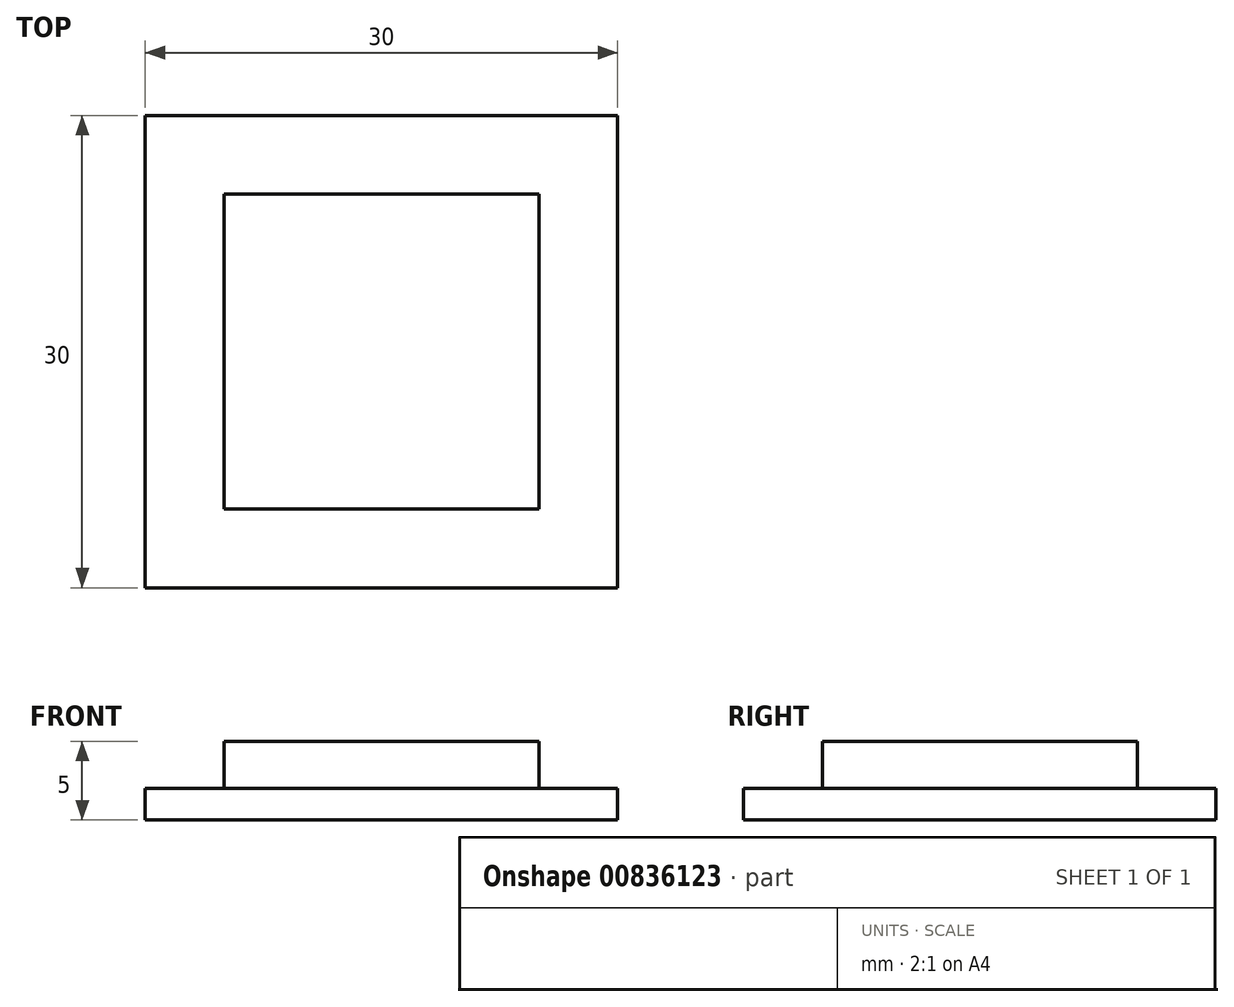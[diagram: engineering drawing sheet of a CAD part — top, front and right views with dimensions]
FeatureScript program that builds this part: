
annotation { "Feature Type Name" : "Feature", "Feature Type Description" : "" }
export const myFeature = defineFeature(function(context is Context, id is Id, definition is map)
    precondition{}
    {
        {
            var Q0;
            Q0=qCreatedBy(makeId("Top.planeOp"),FACE);
            var sketch = newSketch(context, id + "F0", { "sketchPlane" : qUnion([Q0])});
            skLineSegment(sketch, "E0.bottom", {"start": v(15, -15) * mm, "end": v(-15, -15) * mm});
            skLineSegment(sketch, "E0.top", {"start": v(15, 15) * mm, "end": v(-15, 15) * mm});
            skLineSegment(sketch, "E0.left", {"start": v(15, -15) * mm, "end": v(15, 15) * mm});
            skLineSegment(sketch, "E0.right", {"start": v(-15, -15) * mm, "end": v(-15, 15) * mm});
            skPoint(sketch, "E0.middle", {"position": v(0, 0) * mm});
            skSolve(sketch);
        }
        {
            var Q0;
            Q0=makeQuery(id+"F0.imprint","IMPRINT",FACE,{"disambiguationData":[TD([[makeQuery(id+"F0.imprint","IMPRINT",EDGE,{"derivedFrom":sQuery(id+"F0.wireOp",EDGE,"E0.bottom")}),-1.0]])]});
            extrude(context, id + "F1", {"entities" : qUnion([Q0]), "depth" : 5 * mm, "offsetDistance" : 25 * mm});
        }
        {
            var Q0;
            Q0=makeQuery(id+"F1.opExtrude","CAP_FACE",FACE,{"disambiguationData":[OSD([sQuery(id+"F0.wireOp",EDGE,"E0.bottom"),sQuery(id+"F0.wireOp",EDGE,"E0.top"),sQuery(id+"F0.wireOp",EDGE,"E0.left"),sQuery(id+"F0.wireOp",EDGE,"E0.right")])],"isStart":false});
            var sketch = newSketch(context, id + "F2", { "sketchPlane" : qUnion([Q0])});
            skLineSegment(sketch, "E1.bottom", {"start": v(10, -10) * mm, "end": v(-10, -10) * mm});
            skLineSegment(sketch, "E1.top", {"start": v(10, 10) * mm, "end": v(-10, 10) * mm});
            skLineSegment(sketch, "E1.left", {"start": v(10, -10) * mm, "end": v(10, 10) * mm});
            skLineSegment(sketch, "E1.right", {"start": v(-10, -10) * mm, "end": v(-10, 10) * mm});
            skPoint(sketch, "E1.middle", {"position": v(0, 0) * mm});
            skPoint(sketch, "E2.visualSharp", {"position": v(-10, 10) * mm});
            skLineSegment(sketch, "E2.filletArc", {"start": v(-10, 10) * mm, "end": v(-10, 10) * mm});
            skPoint(sketch, "E3.visualSharp", {"position": v(10, 10) * mm});
            skLineSegment(sketch, "E3.filletArc", {"start": v(10, 10) * mm, "end": v(10, 10) * mm});
            skPoint(sketch, "E4.visualSharp", {"position": v(10, -10) * mm});
            skLineSegment(sketch, "E4.filletArc", {"start": v(10, -10) * mm, "end": v(10, -10) * mm});
            skPoint(sketch, "E5.visualSharp", {"position": v(-10, -10) * mm});
            skLineSegment(sketch, "E5.filletArc", {"start": v(-10, -10) * mm, "end": v(-10, -10) * mm});
            skSolve(sketch);
        }
        {
            var Q0;
            Q0=makeQuery(id+"F2.imprint","IMPRINT",FACE,{"disambiguationData":[TD([[makeQuery(id+"F2.imprint","IMPRINT",EDGE,{"derivedFrom":sQuery(id+"F2.wireOp",EDGE,"E1.bottom")}),1.0]])]});
            extrude(context, id + "F3", {"entities" : qUnion([Q0]), "operationType" : NewBodyOperationType.REMOVE, "oppositeDirection" : true, "depth" : 3 * mm, "offsetDistance" : 25 * mm});
        }
    });
